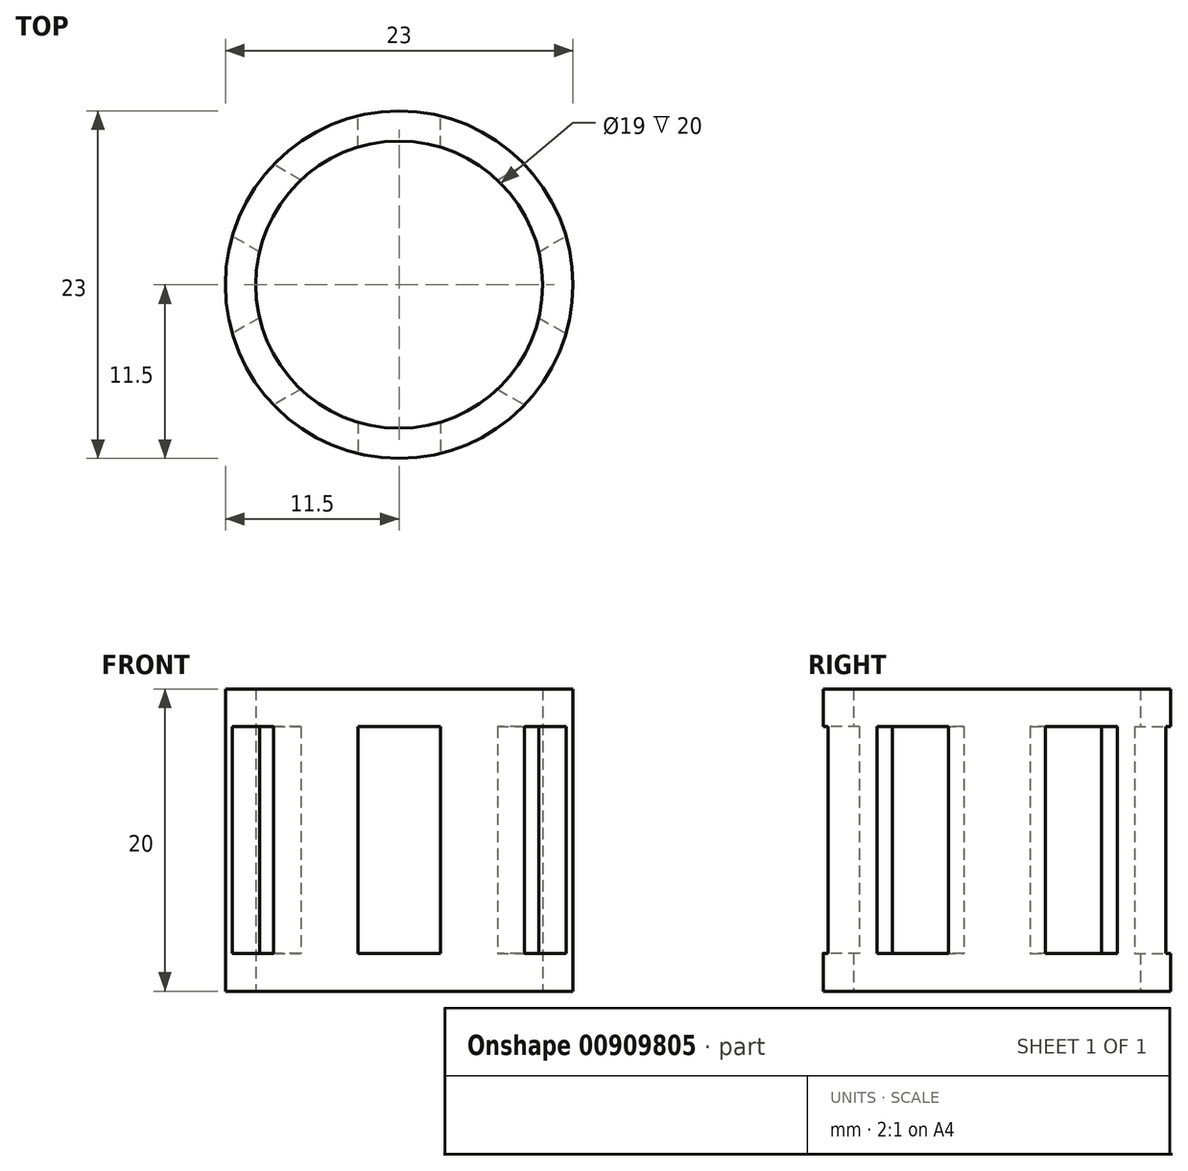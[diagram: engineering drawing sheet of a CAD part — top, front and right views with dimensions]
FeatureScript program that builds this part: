
annotation { "Feature Type Name" : "Feature", "Feature Type Description" : "" }
export const myFeature = defineFeature(function(context is Context, id is Id, definition is map)
    precondition{}
    {
        {
            var Q0;
            Q0=qCreatedBy(makeId("Top.planeOp"),FACE);
            var sketch = newSketch(context, id + "F0", { "sketchPlane" : qUnion([Q0])});
            skCircle(sketch, "E0", {"center": v(0, 0) * mm, "radius": 9.5 * mm});
            skCircle(sketch, "E1", {"center": v(0, 0) * mm, "radius": 11.5 * mm});
            skSolve(sketch);
        }
        {
            var Q0;
            Q0 = qSketchRegion(id + "F0", true);
            extrude(context, id + "F1", {"entities" : qUnion([Q0]), "endBound" : BoundingType.SYMMETRIC, "depth" : 20 * mm, "offsetDistance" : 25 * mm});
        }
        {
            var Q0;
            Q0=qCreatedBy(makeId("Top.planeOp"),FACE);
            var sketch = newSketch(context, id + "F2", { "sketchPlane" : qUnion([Q0])});
            skLineSegment(sketch, "E2.bottom", {"start": v(2.74, 5.97) * mm, "end": v(-2.74, 5.97) * mm});
            skLineSegment(sketch, "E2.top", {"start": v(2.74, 12.31) * mm, "end": v(-2.74, 12.31) * mm});
            skLineSegment(sketch, "E2.left", {"start": v(2.74, 5.97) * mm, "end": v(2.74, 12.31) * mm});
            skLineSegment(sketch, "E2.right", {"start": v(-2.74, 5.97) * mm, "end": v(-2.74, 12.31) * mm});
            skPoint(sketch, "E2.middle", {"position": v(0, 9.14) * mm});
            skPoint(sketch, "E3.1.0", {"position": v(-7.92, 4.57) * mm});
            skLineSegment(sketch, "E3.1.1", {"start": v(-9.3, 8.52) * mm, "end": v(-12.03, 3.79) * mm});
            skLineSegment(sketch, "E3.1.2", {"start": v(-3.8, 5.35) * mm, "end": v(-9.3, 8.52) * mm});
            skLineSegment(sketch, "E3.1.3", {"start": v(-3.8, 5.35) * mm, "end": v(-6.54, 0.62) * mm});
            skLineSegment(sketch, "E3.1.4", {"start": v(-6.54, 0.62) * mm, "end": v(-12.03, 3.79) * mm});
            skPoint(sketch, "E3.2.0", {"position": v(-7.92, -4.57) * mm});
            skLineSegment(sketch, "E3.2.1", {"start": v(-12.03, -3.79) * mm, "end": v(-9.3, -8.52) * mm});
            skLineSegment(sketch, "E3.2.2", {"start": v(-6.54, -0.62) * mm, "end": v(-12.03, -3.79) * mm});
            skLineSegment(sketch, "E3.2.3", {"start": v(-6.54, -0.62) * mm, "end": v(-3.8, -5.35) * mm});
            skLineSegment(sketch, "E3.2.4", {"start": v(-3.8, -5.35) * mm, "end": v(-9.3, -8.52) * mm});
            skPoint(sketch, "E3.3.0", {"position": v(0, -9.14) * mm});
            skLineSegment(sketch, "E3.3.1", {"start": v(-2.74, -12.31) * mm, "end": v(2.74, -12.31) * mm});
            skLineSegment(sketch, "E3.3.2", {"start": v(-2.74, -5.97) * mm, "end": v(-2.74, -12.31) * mm});
            skLineSegment(sketch, "E3.3.3", {"start": v(-2.74, -5.97) * mm, "end": v(2.74, -5.97) * mm});
            skLineSegment(sketch, "E3.3.4", {"start": v(2.74, -5.97) * mm, "end": v(2.74, -12.31) * mm});
            skPoint(sketch, "E3.4.0", {"position": v(7.92, -4.57) * mm});
            skLineSegment(sketch, "E3.4.1", {"start": v(9.3, -8.52) * mm, "end": v(12.03, -3.79) * mm});
            skLineSegment(sketch, "E3.4.2", {"start": v(3.8, -5.35) * mm, "end": v(9.3, -8.52) * mm});
            skLineSegment(sketch, "E3.4.3", {"start": v(3.8, -5.35) * mm, "end": v(6.54, -0.62) * mm});
            skLineSegment(sketch, "E3.4.4", {"start": v(6.54, -0.62) * mm, "end": v(12.03, -3.79) * mm});
            skPoint(sketch, "E3.5.0", {"position": v(7.92, 4.57) * mm});
            skLineSegment(sketch, "E3.5.1", {"start": v(12.03, 3.79) * mm, "end": v(9.3, 8.52) * mm});
            skLineSegment(sketch, "E3.5.2", {"start": v(6.54, 0.62) * mm, "end": v(12.03, 3.79) * mm});
            skLineSegment(sketch, "E3.5.3", {"start": v(6.54, 0.62) * mm, "end": v(3.8, 5.35) * mm});
            skLineSegment(sketch, "E3.5.4", {"start": v(3.8, 5.35) * mm, "end": v(9.3, 8.52) * mm});
            skPoint(sketch, "E3.center", {"position": v(0, 0) * mm});
            skSolve(sketch);
        }
        {
            var Q0;
            Q0 = qSketchRegion(id + "F2", true);
            extrude(context, id + "F3", {"entities" : qUnion([Q0]), "operationType" : NewBodyOperationType.REMOVE, "endBound" : BoundingType.SYMMETRIC, "oppositeDirection" : true, "depth" : 15 * mm, "offsetDistance" : 25 * mm});
        }
        {
            var Q0;
            Q0=makeQuery(id+"F3.boolean.opBoolean","COPY",FACE,{"derivedFrom":makeQuery(id+"F3.opExtrude","CAP_FACE",FACE,{"disambiguationData":[OSD([sQuery(id+"F2.wireOp",EDGE,"E3.3.1"),sQuery(id+"F2.wireOp",EDGE,"E3.3.2"),sQuery(id+"F2.wireOp",EDGE,"E3.3.3"),sQuery(id+"F2.wireOp",EDGE,"E3.3.4")])],"isStart":true})});
            var sketch = newSketch(context, id + "F4", { "sketchPlane" : qUnion([Q0])});
            skCircle(sketch, "E4.0", {"center": v(0, 0) * mm, "radius": 9.5 * mm});
            skCircle(sketch, "E5", {"center": v(0, 0) * mm, "radius": 4 * mm});
            skSolve(sketch);
        }
        {
            var Q0;
            {var subQ0=sQuery(id+"F4.wireOp",EDGE,"E4.0");Q0=makeQuery(id+"F4.imprint","IMPRINT",FACE,{"disambiguationData":[TD([[makeQuery(id+"F4.imprint","IMPRINT",EDGE,{"disambiguationData":[OD(0.0)],"derivedFrom":subQ0}),1.0]])]});}
            var Q1;
            Q1=makeQuery(id+"F1.opExtrude","CAP_FACE",FACE,{"disambiguationData":[OSD([sQuery(id+"F0.wireOp",EDGE,"E0"),sQuery(id+"F0.wireOp",EDGE,"E1")])],"isStart":false});
            extrude(context, id + "F5", {"entities" : qUnion([Q0]), "operationType" : NewBodyOperationType.ADD, "endBound" : BoundingType.UP_TO_SURFACE, "oppositeDirection" : true, "depth" : 25 * mm, "endBoundEntityFace" : qUnion([Q1]), "offsetDistance" : 25 * mm});
        }
    });
